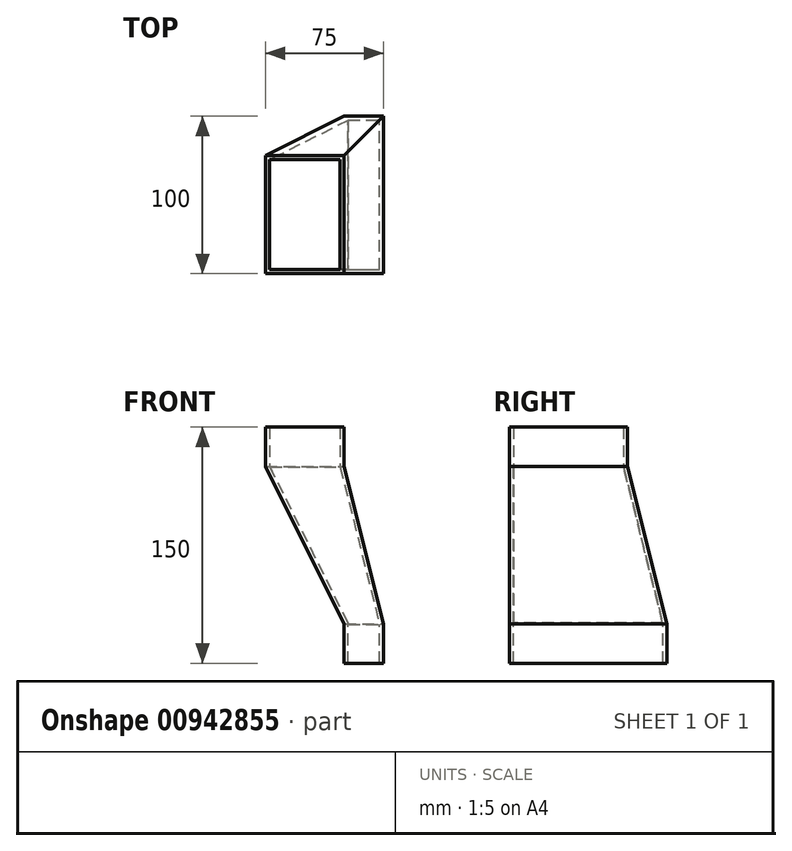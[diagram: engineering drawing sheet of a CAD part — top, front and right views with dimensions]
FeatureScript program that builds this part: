
annotation { "Feature Type Name" : "Feature", "Feature Type Description" : "" }
export const myFeature = defineFeature(function(context is Context, id is Id, definition is map)
    precondition{}
    {
        {
            var Q0;
            Q0=qCreatedBy(makeId("Top.planeOp"),FACE);
            cPlane(context, id + "F0", {"entities" : qUnion([Q0]), "cplaneType" : CPlaneType.OFFSET, "offset" : 100 * mm, "width" : 150 * mm, "height" : 150 * mm});
        }
        {
            var Q0;
            Q0=qCreatedBy(makeId("Top.planeOp"),FACE);
            cPlane(context, id + "F1", {"entities" : qUnion([Q0]), "cplaneType" : CPlaneType.OFFSET, "offset" : 100 * mm, "oppositeDirection" : true, "width" : 150 * mm, "height" : 150 * mm});
        }
        {
            var Q0;
            Q0=qCreatedBy(makeId("Front.planeOp"),FACE);
            cPlane(context, id + "F2", {"entities" : qUnion([Q0]), "cplaneType" : CPlaneType.OFFSET, "offset" : 15 * mm, "oppositeDirection" : true, "width" : 150 * mm, "height" : 150 * mm});
        }
        {
            var Q0;
            Q0=qCreatedBy(id+"F0.planeOp",FACE);
            var sketch = newSketch(context, id + "F3", { "sketchPlane" : qUnion([Q0])});
            skLineSegment(sketch, "E0.bottom", {"start": v(-50, 75) * mm, "end": v(0, 75) * mm});
            skLineSegment(sketch, "E0.top", {"start": v(-50, 0) * mm, "end": v(0, 0) * mm});
            skLineSegment(sketch, "E0.left", {"start": v(-50, 75) * mm, "end": v(-50, 0) * mm});
            skLineSegment(sketch, "E0.right", {"start": v(0, 75) * mm, "end": v(0, 0) * mm});
            skSolve(sketch);
        }
        {
            var Q0;
            Q0=qSketchRegion(id+"F3",true);
            extrude(context, id + "F4", {"entities" : qUnion([Q0]), "depth" : 25 * mm});
        }
        {
            var Q0;
            Q0=qCreatedBy(makeId("Top.planeOp"),FACE);
            var sketch = newSketch(context, id + "F5", { "sketchPlane" : qUnion([Q0])});
            skLineSegment(sketch, "E1.bottom", {"start": v(0, 0) * mm, "end": v(25, 0) * mm});
            skLineSegment(sketch, "E1.top", {"start": v(0, 100) * mm, "end": v(25, 100) * mm});
            skLineSegment(sketch, "E1.left", {"start": v(0, 0) * mm, "end": v(0, 100) * mm});
            skLineSegment(sketch, "E1.right", {"start": v(25, 0) * mm, "end": v(25, 100) * mm});
            skSolve(sketch);
        }
        {
            var Q0;
            Q0=qCreatedBy(id+"F1.planeOp",FACE);
            var sketch = newSketch(context, id + "F6", { "sketchPlane" : qUnion([Q0])});
            skArc(sketch, "E2", {"start": v(-25.82, -27.2) * mm, "mid": v(1.4, -37.47) * mm, "end": v(27.78, -25.19) * mm});
            skArc(sketch, "E3", {"start": v(27.78, -25.19) * mm, "mid": v(37.43, 2.33) * mm, "end": v(24.44, 28.44) * mm});
            skArc(sketch, "E4", {"start": v(24.44, 28.44) * mm, "mid": v(2.13, 37.44) * mm, "end": v(-21.06, 31.03) * mm});
            skArc(sketch, "E5", {"start": v(-21.06, 31.03) * mm, "mid": v(-37.38, 3.05) * mm, "end": v(-25.82, -27.2) * mm});
            skSolve(sketch);
        }
        {
            var Q0;
            Q0=qCreatedBy(id+"F2.planeOp",FACE);
            var sketch = newSketch(context, id + "F7", { "sketchPlane" : qUnion([Q0])});
            skFitSpline(sketch, "E6", {"points": [v(34.37, -100) * mm, v(25, 0) * mm, v(0, 100) * mm], "startDerivative": vector(144.98, 133.2) * mm, "endDerivative": vector(-251.79, 197.32) * mm});
            skFitSpline(sketch, "E7", {"points": [v(-34.37, -100) * mm, v(0, 0) * mm, v(-50, 100) * mm], "startDerivative": vector(-32.66, 191.05) * mm, "endDerivative": vector(55.72, 190.81) * mm});
            skSolve(sketch);
        }
        {
            var Q0;
            Q0=makeQuery(id+"F5.imprint","IMPRINT",FACE,{"disambiguationData":[TD([[makeQuery(id+"F5.imprint","IMPRINT",EDGE,{"derivedFrom":sQuery(id+"F5.wireOp",EDGE,"E1.bottom")}),1.0]])]});
            extrude(context, id + "F8", {"entities" : qUnion([Q0]), "oppositeDirection" : true, "depth" : 25 * mm});
        }
        {
            var Q0;
            Q0=makeQuery(id+"F4.opExtrude","CAP_FACE",FACE,{"disambiguationData":[OSD([sQuery(id+"F3.wireOp",EDGE,"E0.bottom"),sQuery(id+"F3.wireOp",EDGE,"E0.top"),sQuery(id+"F3.wireOp",EDGE,"E0.left"),sQuery(id+"F3.wireOp",EDGE,"E0.right")])],"isStart":true});
            var Q1;
            Q1=makeQuery(id+"F5.imprint","IMPRINT",FACE,{"disambiguationData":[TD([[makeQuery(id+"F5.imprint","IMPRINT",EDGE,{"derivedFrom":sQuery(id+"F5.wireOp",EDGE,"E1.bottom")}),1.0]])]});
            var Q2;
            Q2=sQuery(id+"F5.wireOp",VERTEX,"E1.right.end");
            var Q3;
            Q3=makeQuery(id+"F4.opExtrude","CAP_VERTEX",VERTEX,{"disambiguationData":[OSD([sQuery(id+"F3.wireOp",EDGE,"E0.bottom"),sQuery(id+"F3.wireOp",EDGE,"E0.right")])],"isStart":true});
            loft(context, id + "F9", {"operationType" : NewBodyOperationType.ADD, "sheetProfilesArray" : [{ "sheetProfileEntities" : qUnion([Q0]) }, { "sheetProfileEntities" : qUnion([Q1]) }], "matchConnections" : true, "connections" : [{ "connectionEntities" : qUnion([Q2, Q3]), "connectionEdgeQueries" : qUnion([]), "connectionEdgeParameters" : [] }]});
        }
        {
            var Q0;
            Q0=makeQuery(id+"F4.opExtrude","CAP_FACE",FACE,{"disambiguationData":[OSD([sQuery(id+"F3.wireOp",EDGE,"E0.bottom"),sQuery(id+"F3.wireOp",EDGE,"E0.top"),sQuery(id+"F3.wireOp",EDGE,"E0.left"),sQuery(id+"F3.wireOp",EDGE,"E0.right")])],"isStart":false});
            var Q1;
            Q1=makeQuery(id+"F8.opExtrude","CAP_FACE",FACE,{"disambiguationData":[OSD([sQuery(id+"F5.wireOp",EDGE,"E1.bottom"),sQuery(id+"F5.wireOp",EDGE,"E1.top"),sQuery(id+"F5.wireOp",EDGE,"E1.left"),sQuery(id+"F5.wireOp",EDGE,"E1.right")])],"isStart":false});
            shell(context, id + "F10", {"entities" : qUnion([Q0, Q1]), "thickness" : 2.5 * mm});
        }
    });
